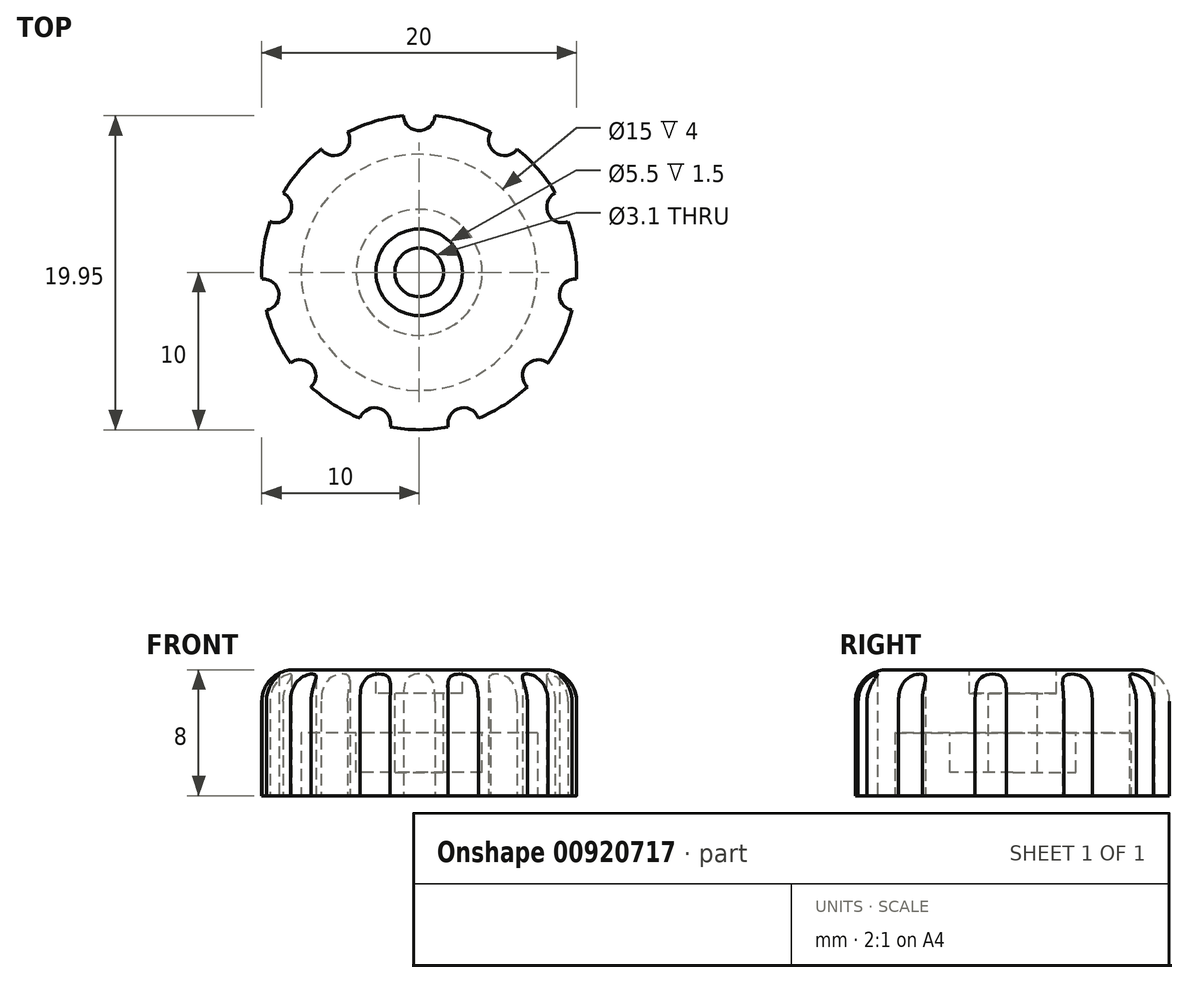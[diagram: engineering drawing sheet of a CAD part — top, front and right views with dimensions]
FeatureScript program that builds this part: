
annotation { "Feature Type Name" : "Feature", "Feature Type Description" : "" }
export const myFeature = defineFeature(function(context is Context, id is Id, definition is map)
    precondition{}
    {
        {
            var Q0;
            Q0=qCreatedBy(makeId("Top.planeOp"),FACE);
            var sketch = newSketch(context, id + "F0", { "sketchPlane" : qUnion([Q0])});
            skCircle(sketch, "E0", {"center": v(0, 0) * mm, "radius": 10 * mm});
            skSolve(sketch);
        }
        {
            var Q0;
            Q0=makeQuery(id+"F0.imprint","IMPRINT",FACE,{"disambiguationData":[TD([[makeQuery(id+"F0.imprint","IMPRINT",EDGE,{"derivedFrom":sQuery(id+"F0.wireOp",EDGE,"E0")}),1.0]])]});
            extrude(context, id + "F1", {"entities" : qUnion([Q0]), "depth" : 8 * mm, "offsetDistance" : 25 * mm});
        }
        {
            var Q0;
            Q0=qCreatedBy(makeId("Top.planeOp"),FACE);
            var sketch = newSketch(context, id + "F2", { "sketchPlane" : qUnion([Q0])});
            skCircle(sketch, "E1", {"center": v(0, 0) * mm, "radius": 7.5 * mm});
            skSolve(sketch);
        }
        {
            var Q0;
            Q0 = qSketchRegion(id + "F2", true);
            extrude(context, id + "F3", {"entities" : qUnion([Q0]), "operationType" : NewBodyOperationType.REMOVE, "flatOperationType" : FlatOperationType.REMOVE, "depth" : 4 * mm, "offsetDistance" : 25 * mm, "domain" : OperationDomain.MODEL});
        }
        {
            var Q0;
            Q0=makeQuery(id+"F3.boolean.opBoolean","COPY",FACE,{"derivedFrom":makeQuery(id+"F3.opExtrude","CAP_FACE",FACE,{"disambiguationData":[OSD([sQuery(id+"F2.wireOp",EDGE,"E1")])],"isStart":false})});
            var sketch = newSketch(context, id + "F4", { "sketchPlane" : qUnion([Q0])});
            skCircle(sketch, "E2", {"center": v(0, 0) * mm, "radius": 4 * mm});
            skSolve(sketch);
        }
        {
            var Q0;
            Q0=makeQuery(id+"F4.imprint","IMPRINT",FACE,{"disambiguationData":[TD([[makeQuery(id+"F4.imprint","IMPRINT",EDGE,{"derivedFrom":sQuery(id+"F4.wireOp",EDGE,"E2")}),1.0]])]});
            extrude(context, id + "F5", {"entities" : qUnion([Q0]), "operationType" : NewBodyOperationType.ADD, "flatOperationType" : FlatOperationType.REMOVE, "depth" : 2.5 * mm, "offsetDistance" : 25 * mm, "domain" : OperationDomain.MODEL});
        }
        {
            var Q0;
            Q0=makeQuery(id+"F1.opExtrude","CAP_EDGE",EDGE,{"disambiguationData":[OSD([sQuery(id+"F0.wireOp",EDGE,"E0")])],"isStart":false});
            fillet(context, id + "F6", {"entities" : qUnion([Q0]), "radius" : 2 * mm, "tangentPropagation" : true, "allowEdgeOverflow" : false});
        }
        {
            var Q0;
            Q0=makeQuery(id+"F1.opExtrude","CAP_FACE",FACE,{"disambiguationData":[OSD([sQuery(id+"F0.wireOp",EDGE,"E0")])],"isStart":false});
            var sketch = newSketch(context, id + "F7", { "sketchPlane" : qUnion([Q0])});
            skCircle(sketch, "E3", {"center": v(0, 0) * mm, "radius": 2.75 * mm});
            skSolve(sketch);
        }
        {
            var Q0;
            Q0=makeQuery(id+"F7.imprint","IMPRINT",FACE,{"disambiguationData":[TD([[makeQuery(id+"F7.imprint","IMPRINT",EDGE,{"derivedFrom":sQuery(id+"F7.wireOp",EDGE,"E3")}),1.0]])]});
            extrude(context, id + "F8", {"entities" : qUnion([Q0]), "operationType" : NewBodyOperationType.REMOVE, "oppositeDirection" : true, "depth" : 1.5 * mm, "offsetDistance" : 25 * mm});
        }
        {
            var Q0;
            Q0=makeQuery(id+"F1.opExtrude","CAP_FACE",FACE,{"disambiguationData":[OSD([sQuery(id+"F0.wireOp",EDGE,"E0")])],"isStart":false});
            var sketch = newSketch(context, id + "F9", { "sketchPlane" : qUnion([Q0])});
            skCircle(sketch, "E4", {"center": v(0, 0) * mm, "radius": 1.55 * mm});
            skSolve(sketch);
        }
        {
            var Q0;
            Q0=makeQuery(id+"F9.imprint","IMPRINT",FACE,{"disambiguationData":[TD([[makeQuery(id+"F9.imprint","IMPRINT",EDGE,{"derivedFrom":sQuery(id+"F9.wireOp",EDGE,"E4")}),1.0]])]});
            extrude(context, id + "F10", {"entities" : qUnion([Q0]), "operationType" : NewBodyOperationType.REMOVE, "endBound" : BoundingType.THROUGH_ALL, "oppositeDirection" : true, "depth" : 25 * mm, "offsetDistance" : 25 * mm});
        }
        {
            var Q0;
            Q0=qCreatedBy(makeId("Top.planeOp"),FACE);
            var sketch = newSketch(context, id + "F11", { "sketchPlane" : qUnion([Q0])});
            skCircle(sketch, "E5", {"center": v(0, 10) * mm, "radius": 1 * mm});
            skCircle(sketch, "E6.1.0", {"center": v(-5.4, 8.41) * mm, "radius": 1 * mm});
            skCircle(sketch, "E6.2.0", {"center": v(-9.1, 4.15) * mm, "radius": 1 * mm});
            skCircle(sketch, "E6.3.0", {"center": v(-9.9, -1.42) * mm, "radius": 1 * mm});
            skCircle(sketch, "E6.4.0", {"center": v(-7.56, -6.55) * mm, "radius": 1 * mm});
            skCircle(sketch, "E6.5.0", {"center": v(-2.82, -9.6) * mm, "radius": 1 * mm});
            skCircle(sketch, "E6.6.0", {"center": v(2.82, -9.6) * mm, "radius": 1 * mm});
            skCircle(sketch, "E6.7.0", {"center": v(7.56, -6.55) * mm, "radius": 1 * mm});
            skCircle(sketch, "E6.8.0", {"center": v(9.9, -1.42) * mm, "radius": 1 * mm});
            skCircle(sketch, "E6.9.0", {"center": v(9.1, 4.15) * mm, "radius": 1 * mm});
            skPoint(sketch, "E6.center", {"position": v(0, 0) * mm});
            skCircle(sketch, "E7.1.10.0", {"center": v(5.4, 8.41) * mm, "radius": 1 * mm});
            skSolve(sketch);
        }
        {
            var Q0;
            Q0 = qSketchRegion(id + "F11", true);
            extrude(context, id + "F12", {"entities" : qUnion([Q0]), "operationType" : NewBodyOperationType.REMOVE, "endBound" : BoundingType.THROUGH_ALL, "depth" : 25 * mm, "offsetDistance" : 25 * mm});
        }
    });
